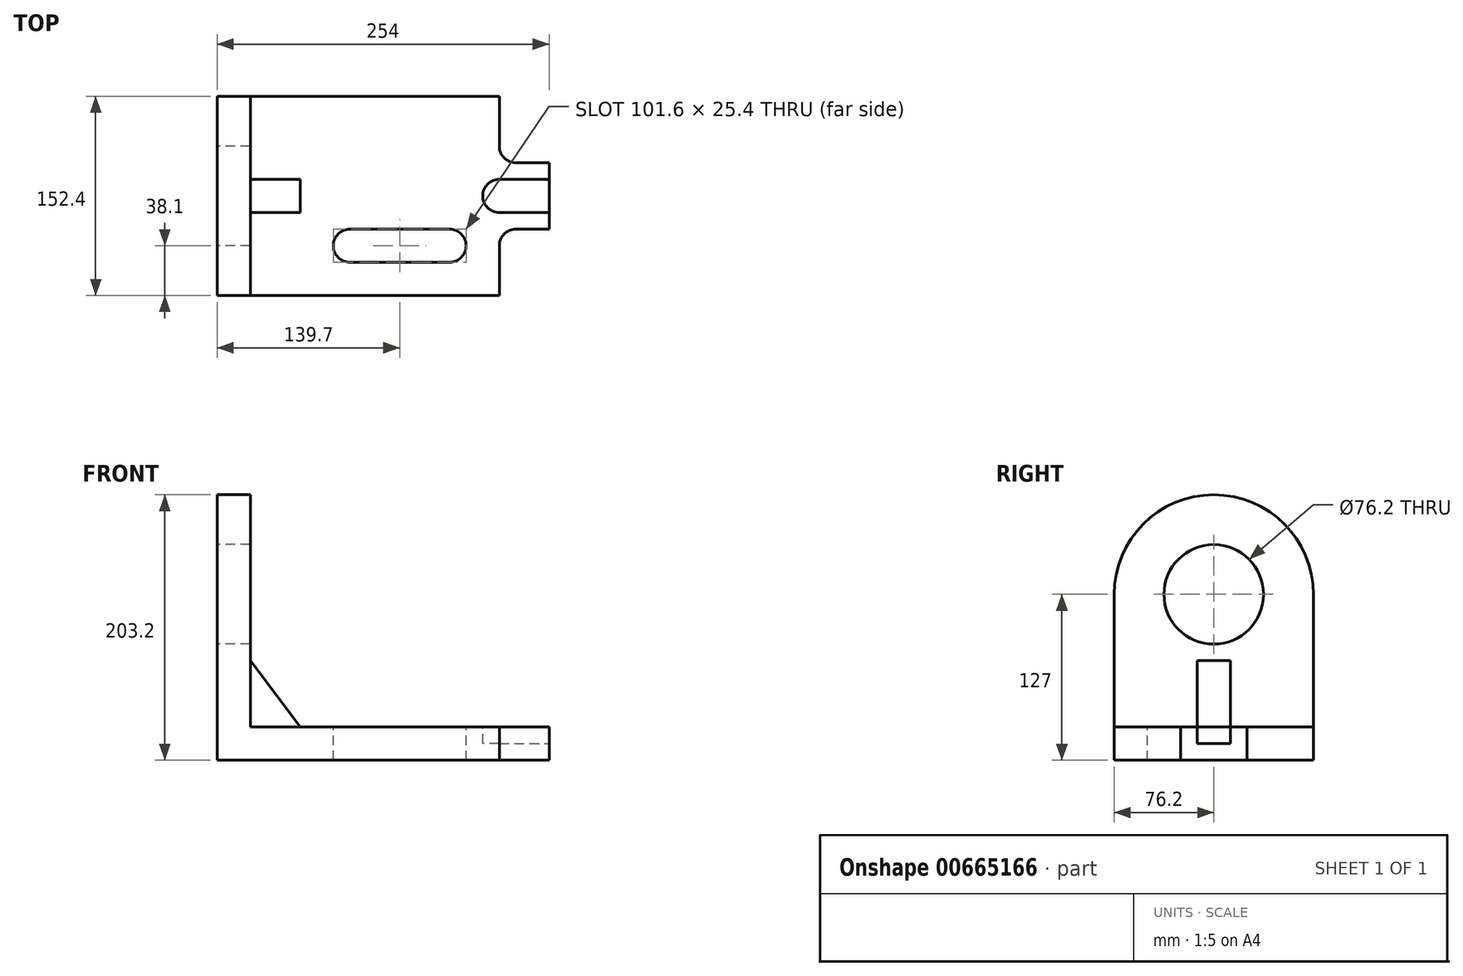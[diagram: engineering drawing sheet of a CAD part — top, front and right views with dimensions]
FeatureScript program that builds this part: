
annotation { "Feature Type Name" : "Feature", "Feature Type Description" : "" }
export const myFeature = defineFeature(function(context is Context, id is Id, definition is map)
    precondition{}
    {
        {
            var Q0;
            Q0=qCreatedBy(makeId("Front.planeOp"),FACE);
            var sketch = newSketch(context, id + "F0", { "sketchPlane" : qUnion([Q0])});
            skLineSegment(sketch, "E0", {"start": v(0, 203.2) * mm, "end": v(0, 0) * mm});
            skLineSegment(sketch, "E1", {"start": v(0, 0) * mm, "end": v(254, 0) * mm});
            skLineSegment(sketch, "E2", {"start": v(254, 0) * mm, "end": v(254, 12.7) * mm});
            skLineSegment(sketch, "E3", {"start": v(254, 12.7) * mm, "end": v(254, 12.7) * mm});
            skLineSegment(sketch, "E4", {"start": v(254, 12.7) * mm, "end": v(254, 25.4) * mm});
            skLineSegment(sketch, "E5", {"start": v(254, 25.4) * mm, "end": v(25.4, 25.4) * mm});
            skLineSegment(sketch, "E6", {"start": v(25.4, 25.4) * mm, "end": v(25.4, 203.2) * mm});
            skLineSegment(sketch, "E7", {"start": v(25.4, 203.2) * mm, "end": v(0, 203.2) * mm});
            skLineSegment(sketch, "E8", {"start": v(25.4, 76.2) * mm, "end": v(63.5, 25.4) * mm});
            skSolve(sketch);
        }
        {
            var Q0;
            Q0=makeQuery(id+"F0.imprint","IMPRINT",FACE,{"disambiguationData":[TD([[makeQuery(id+"F0.imprint","IMPRINT",EDGE,{"derivedFrom":sQuery(id+"F0.wireOp",EDGE,"E0")}),1.0]])]});
            extrude(context, id + "F1", {"entities" : qUnion([Q0]), "endBound" : BoundingType.SYMMETRIC, "depth" : 152.4 * mm, "offsetDistance" : 25.4 * mm});
        }
        {
            var Q0;
            Q0=makeQuery(id+"F1.opExtrude","SWEPT_FACE",FACE,{"disambiguationData":[OSD([sQuery(id+"F0.wireOp",EDGE,"E5")])]});
            var sketch = newSketch(context, id + "F2", { "sketchPlane" : qUnion([Q0])});
            skArc(sketch, "E9", {"start": v(177.8, -50.8) * mm, "mid": v(190.5, -38.1) * mm, "end": v(177.8, -25.4) * mm});
            skArc(sketch, "E10", {"start": v(101.6, -25.4) * mm, "mid": v(88.9, -38.1) * mm, "end": v(101.6, -50.8) * mm});
            skLineSegment(sketch, "E11", {"start": v(101.6, -25.4) * mm, "end": v(177.8, -25.4) * mm});
            skLineSegment(sketch, "E12", {"start": v(101.6, -50.8) * mm, "end": v(177.8, -50.8) * mm});
            skLineSegment(sketch, "E13.0", {"start": v(215.9, -76.2) * mm, "end": v(215.9, -25.4) * mm});
            skArc(sketch, "E14", {"start": v(215.9, 12.7) * mm, "mid": v(203.2, 0) * mm, "end": v(215.9, -12.7) * mm});
            skLineSegment(sketch, "E15", {"start": v(215.9, 12.7) * mm, "end": v(254, 12.7) * mm});
            skLineSegment(sketch, "E16", {"start": v(215.9, -12.7) * mm, "end": v(254, -12.7) * mm});
            skLineSegment(sketch, "E17.trimOffspring", {"start": v(215.9, 25.4) * mm, "end": v(215.9, 76.2) * mm});
            skPoint(sketch, "E18.orphan", {"position": v(254, 0) * mm});
            skLineSegment(sketch, "E19.0", {"start": v(215.9, 25.4) * mm, "end": v(254, 25.4) * mm});
            skLineSegment(sketch, "E20.0", {"start": v(215.9, -25.4) * mm, "end": v(254, -25.4) * mm});
            skSolve(sketch);
        }
        {
            var Q0;
            {var subQ1=sQuery(id+"F2.wireOp",EDGE,"E15");Q0=makeQuery(id+"F2.imprint","IMPRINT",FACE,{"disambiguationData":[TD([[makeQuery(id+"F2.imprint","IMPRINT",EDGE,{"derivedFrom":subQ1}),-1.0]])]});}
            extrude(context, id + "F3", {"entities" : qUnion([Q0]), "operationType" : NewBodyOperationType.REMOVE, "oppositeDirection" : true, "depth" : 12.7 * mm, "offsetDistance" : 25.4 * mm});
        }
        {
            var Q0;
            {var subQ0=sQuery(id+"F2.wireOp",EDGE,"E15");Q0=makeQuery(id+"F2.imprint","IMPRINT",FACE,{"disambiguationData":[TD([[makeQuery(id+"F2.imprint","IMPRINT",EDGE,{"derivedFrom":subQ0}),1.0]])]});}
            var Q1;
            {var subQ0=sQuery(id+"F2.wireOp",EDGE,"E13.0");Q1=makeQuery(id+"F2.imprint","IMPRINT",FACE,{"disambiguationData":[TD([[makeQuery(id+"F2.imprint","IMPRINT",EDGE,{"derivedFrom":subQ0}),-1.0]])]});}
            var Q2;
            Q2=makeQuery(id+"F2.imprint","IMPRINT",FACE,{"disambiguationData":[TD([[makeQuery(id+"F2.imprint","IMPRINT",EDGE,{"derivedFrom":sQuery(id+"F2.wireOp",EDGE,"E9")}),1.0]])]});
            var Q3;
            Q3=makeQuery(id+"F2.imprint","IMPRINT",FACE,{"disambiguationData":[TD([[makeQuery(id+"F2.imprint","IMPRINT",EDGE,{"derivedFrom":sQuery(id+"F2.wireOp",EDGE,"VmA8LWpB-pt0t-r2IS-otfY-BIBfEy8VWQtf")}),1.0]])]});
            extrude(context, id + "F4", {"entities" : qUnion([Q0, Q1, Q2, Q3]), "operationType" : NewBodyOperationType.ADD, "oppositeDirection" : true, "depth" : 25.4 * mm, "offsetDistance" : 25.4 * mm});
        }
        {
            var Q0;
            {var subQ0=sQuery(id+"F2.wireOp",EDGE,"E13.0");Q0=makeQuery(id+"F2.imprint","IMPRINT",FACE,{"disambiguationData":[TD([[makeQuery(id+"F2.imprint","IMPRINT",EDGE,{"derivedFrom":subQ0}),-1.0]])]});}
            var Q1;
            {var subQ0=sQuery(id+"F2.wireOp",EDGE,"E17.trimOffspring");Q1=makeQuery(id+"F2.imprint","IMPRINT",FACE,{"disambiguationData":[TD([[makeQuery(id+"F2.imprint","IMPRINT",EDGE,{"derivedFrom":subQ0}),-1.0]])]});}
            extrude(context, id + "F5", {"entities" : qUnion([Q0, Q1]), "operationType" : NewBodyOperationType.REMOVE, "oppositeDirection" : true, "depth" : 25.4 * mm, "offsetDistance" : 25.4 * mm});
        }
        {
            var Q0;
            Q0=makeQuery(id+"F5.boolean.opBoolean","COPY",EDGE,{"derivedFrom":makeQuery(id+"F5.opExtrude","SWEPT_EDGE",EDGE,{"disambiguationData":[OSD([sQuery(id+"F2.wireOp",EDGE,"E13.0"),sQuery(id+"F2.wireOp",EDGE,"E20.0")])]})});
            var Q1;
            Q1=makeQuery(id+"F5.boolean.opBoolean","COPY",EDGE,{"derivedFrom":makeQuery(id+"F5.opExtrude","SWEPT_EDGE",EDGE,{"disambiguationData":[OSD([sQuery(id+"F0.wireOp",EDGE,"E5"),sQuery(id+"F2.wireOp",EDGE,"E13.0")])]})});
            var Q2;
            Q2=makeQuery(id+"F5.boolean.opBoolean","COPY",EDGE,{"derivedFrom":makeQuery(id+"F5.opExtrude","SWEPT_EDGE",EDGE,{"disambiguationData":[OSD([sQuery(id+"F2.wireOp",EDGE,"E17.trimOffspring"),sQuery(id+"F2.wireOp",EDGE,"E19.0")])]})});
            var Q3;
            Q3=makeQuery(id+"F5.boolean.opBoolean","COPY",EDGE,{"derivedFrom":makeQuery(id+"F5.opExtrude","SWEPT_EDGE",EDGE,{"disambiguationData":[OSD([sQuery(id+"F0.wireOp",EDGE,"E5"),sQuery(id+"F2.wireOp",EDGE,"E17.trimOffspring")])]})});
            fillet(context, id + "F6", {"entities" : qUnion([Q0, Q1, Q2, Q3]), "radius" : 12.7 * mm, "tangentPropagation" : true, "allowEdgeOverflow" : false});
        }
        {
            var Q0;
            Q0=makeQuery(id+"F1.opExtrude","SWEPT_FACE",FACE,{"disambiguationData":[OSD([sQuery(id+"F0.wireOp",EDGE,"E0")])]});
            var sketch = newSketch(context, id + "F7", { "sketchPlane" : qUnion([Q0])});
            skArc(sketch, "E21", {"start": v(76.2, 127) * mm, "mid": v(0, 203.2) * mm, "end": v(-76.2, 127) * mm});
            skCircle(sketch, "E22", {"center": v(0, 127) * mm, "radius": 38.1 * mm});
            skSolve(sketch);
        }
        {
            var Q0;
            {var subQ0=sQuery(id+"F7.wireOp",EDGE,"E21");var subQ1=sQuery(id+"F0.wireOp",EDGE,"E0");var subQ2=makeQuery(id+"F1.opExtrude","CAP_EDGE",EDGE,{"disambiguationData":[OSD([subQ1])],"isStart":false});var subQ3=makeQuery(id+"F7.imprint","INTERSECT",VERTEX,{"derivedFrom":[subQ2,subQ0]});Q0=makeQuery(id+"F7.imprint","IMPRINT",FACE,{"disambiguationData":[TD([[makeQuery(id+"F7.imprint","IMPRINT",EDGE,{"disambiguationData":[TD([[subQ3,-1.0]])],"derivedFrom":subQ0}),-1.0]])]});}
            var Q1;
            Q1=makeQuery(id+"F7.imprint","IMPRINT",FACE,{"disambiguationData":[TD([[makeQuery(id+"F7.imprint","IMPRINT",EDGE,{"derivedFrom":sQuery(id+"F7.wireOp",EDGE,"E22")}),1.0]])]});
            var Q2;
            {var subQ0=sQuery(id+"F7.wireOp",EDGE,"E21");var subQ1=sQuery(id+"F0.wireOp",EDGE,"E0");var subQ2=makeQuery(id+"F1.opExtrude","CAP_EDGE",EDGE,{"disambiguationData":[OSD([subQ1])],"isStart":true});var subQ3=makeQuery(id+"F7.imprint","INTERSECT",VERTEX,{"derivedFrom":[subQ2,subQ0]});Q2=makeQuery(id+"F7.imprint","IMPRINT",FACE,{"disambiguationData":[TD([[makeQuery(id+"F7.imprint","IMPRINT",EDGE,{"disambiguationData":[TD([[subQ3,1.0]])],"derivedFrom":subQ0}),-1.0]])]});}
            extrude(context, id + "F8", {"entities" : qUnion([Q0, Q1, Q2]), "operationType" : NewBodyOperationType.REMOVE, "oppositeDirection" : true, "depth" : 25.4 * mm, "offsetDistance" : 25.4 * mm});
        }
        {
            var Q0;
            Q0=makeQuery(id+"F2.imprint","IMPRINT",FACE,{"disambiguationData":[TD([[makeQuery(id+"F2.imprint","IMPRINT",EDGE,{"derivedFrom":sQuery(id+"F2.wireOp",EDGE,"E9")}),1.0]])]});
            extrude(context, id + "F9", {"entities" : qUnion([Q0]), "operationType" : NewBodyOperationType.REMOVE, "endBound" : BoundingType.THROUGH_ALL, "oppositeDirection" : true, "depth" : 25.4 * mm, "offsetDistance" : 25.4 * mm});
        }
        {
            var Q0;
            {var subQ3=sQuery(id+"F0.wireOp",EDGE,"E8");Q0=makeQuery(id+"F0.imprint","IMPRINT",FACE,{"disambiguationData":[TD([[makeQuery(id+"F0.imprint","IMPRINT",EDGE,{"derivedFrom":subQ3}),-1.0]])]});}
            extrude(context, id + "F10", {"entities" : qUnion([Q0]), "operationType" : NewBodyOperationType.ADD, "endBound" : BoundingType.SYMMETRIC, "depth" : 25.4 * mm, "offsetDistance" : 25.4 * mm});
        }
    });
